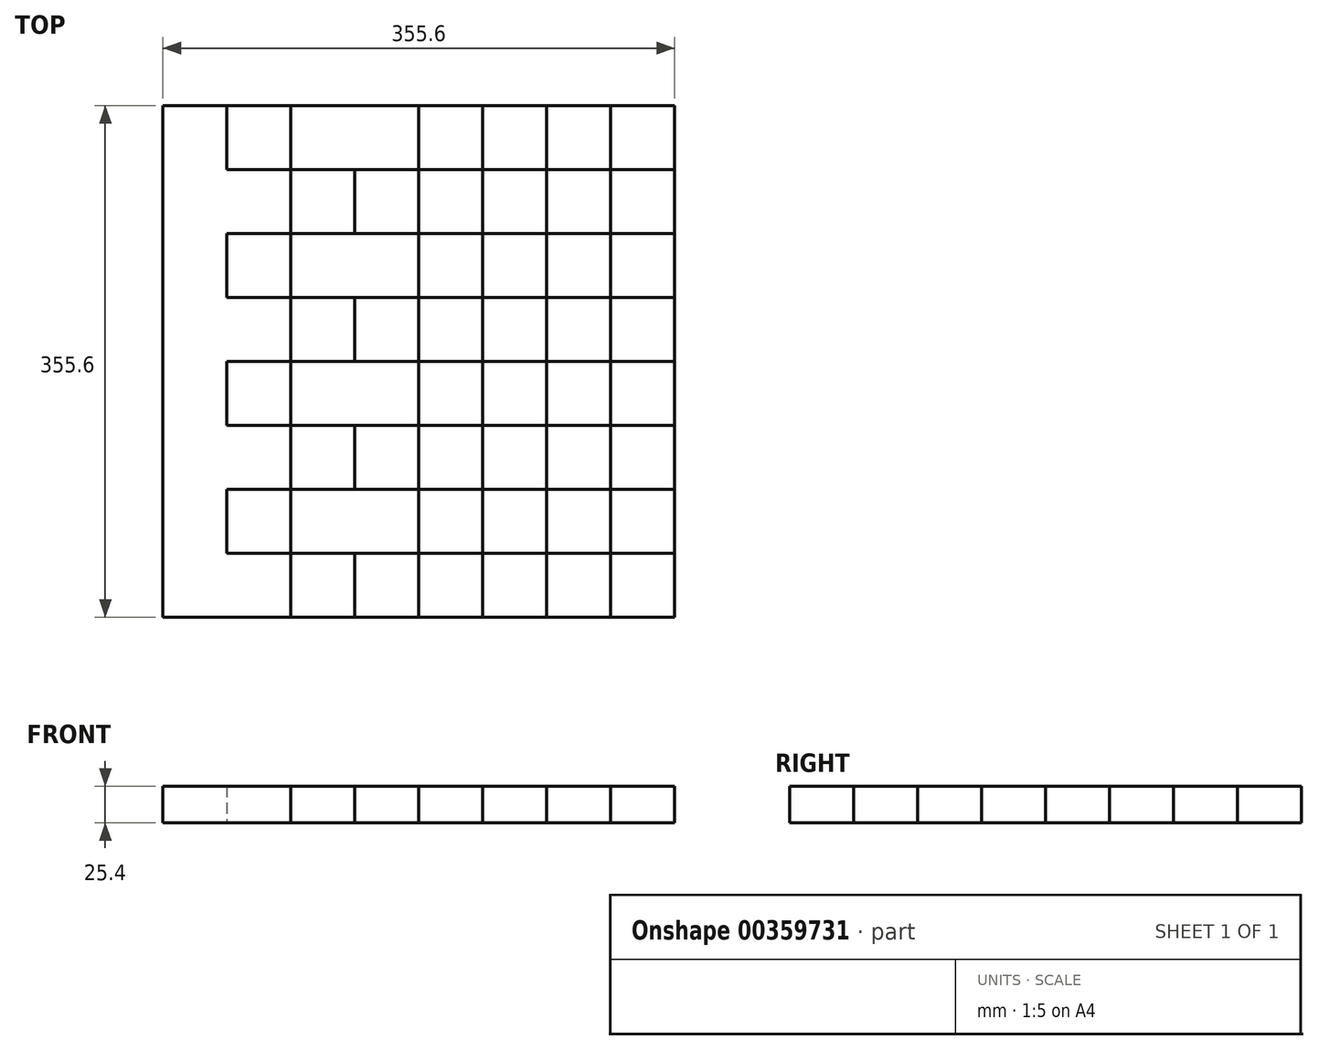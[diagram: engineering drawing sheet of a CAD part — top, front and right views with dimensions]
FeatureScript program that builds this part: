
annotation { "Feature Type Name" : "Feature", "Feature Type Description" : "" }
export const myFeature = defineFeature(function(context is Context, id is Id, definition is map)
    precondition{}
    {
        {
            var Q0;
            Q0=qCreatedBy(makeId("Top.planeOp"),FACE);
            var sketch = newSketch(context, id + "F0", { "sketchPlane" : qUnion([Q0])});
            skLineSegment(sketch, "E0.bottom", {"start": v(177.8, 177.8) * mm, "end": v(-177.8, 177.8) * mm});
            skLineSegment(sketch, "E0.top", {"start": v(177.8, -177.8) * mm, "end": v(-177.8, -177.8) * mm});
            skLineSegment(sketch, "E0.left", {"start": v(177.8, 177.8) * mm, "end": v(177.8, -177.8) * mm});
            skLineSegment(sketch, "E0.right", {"start": v(-177.8, 177.8) * mm, "end": v(-177.8, -177.8) * mm});
            skPoint(sketch, "E0.middle", {"position": v(0, 0) * mm});
            skLineSegment(sketch, "E1", {"start": v(-133.35, 177.8) * mm, "end": v(-133.35, -177.8) * mm});
            skLineSegment(sketch, "E2", {"start": v(-88.9, -177.8) * mm, "end": v(-88.9, 177.8) * mm});
            skLineSegment(sketch, "E3", {"start": v(-44.45, -177.8) * mm, "end": v(-44.45, 177.8) * mm});
            skLineSegment(sketch, "E4", {"start": v(0, 177.8) * mm, "end": v(0, -177.8) * mm});
            skLineSegment(sketch, "E5", {"start": v(0, -177.8) * mm, "end": v(0, 177.8) * mm});
            skLineSegment(sketch, "E6.MirrorCS", {"start": v(44.45, -177.8) * mm, "end": v(44.45, 177.8) * mm});
            skLineSegment(sketch, "E7.MirrorCS", {"start": v(88.9, -177.8) * mm, "end": v(88.9, 177.8) * mm});
            skLineSegment(sketch, "E8.MirrorCS", {"start": v(133.35, 177.8) * mm, "end": v(133.35, -177.8) * mm});
            skLineSegment(sketch, "E9", {"start": v(0, 0) * mm, "end": v(-177.8, 0) * mm});
            skLineSegment(sketch, "E10", {"start": v(-177.8, 0) * mm, "end": v(177.8, 0) * mm});
            skLineSegment(sketch, "E11", {"start": v(-177.8, 44.45) * mm, "end": v(177.8, 44.45) * mm});
            skLineSegment(sketch, "E12", {"start": v(177.8, 88.9) * mm, "end": v(-177.8, 88.9) * mm});
            skLineSegment(sketch, "E13", {"start": v(-177.8, 133.35) * mm, "end": v(177.8, 133.35) * mm});
            skLineSegment(sketch, "E14.MirrorCS", {"start": v(-177.8, -44.45) * mm, "end": v(177.8, -44.45) * mm});
            skLineSegment(sketch, "E15.MirrorCS", {"start": v(177.8, -88.9) * mm, "end": v(-177.8, -88.9) * mm});
            skLineSegment(sketch, "E16.MirrorCS", {"start": v(-177.8, -133.35) * mm, "end": v(177.8, -133.35) * mm});
            skSolve(sketch);
        }
        {
            var Q0;
            {var subQ0=sQuery(id+"F0.wireOp",EDGE,"E1");var subQ1=sQuery(id+"F0.wireOp",EDGE,"E0.top");var subQ2=makeQuery(id+"F0.imprint","INTERSECT",VERTEX,{"derivedFrom":[subQ1,subQ0]});Q0=makeQuery(id+"F0.imprint","IMPRINT",FACE,{"disambiguationData":[TD([[makeQuery(id+"F0.imprint","IMPRINT",EDGE,{"disambiguationData":[TD([[subQ2,1.0]])],"derivedFrom":subQ1}),-1.0]])]});}
            var Q1;
            {var subQ0=sQuery(id+"F0.wireOp",EDGE,"E3");var subQ1=sQuery(id+"F0.wireOp",EDGE,"E0.top");var subQ2=makeQuery(id+"F0.imprint","INTERSECT",VERTEX,{"derivedFrom":[subQ1,subQ0]});Q1=makeQuery(id+"F0.imprint","IMPRINT",FACE,{"disambiguationData":[TD([[makeQuery(id+"F0.imprint","IMPRINT",EDGE,{"disambiguationData":[TD([[subQ2,1.0]])],"derivedFrom":subQ1}),-1.0]])]});}
            var Q2;
            {var subQ0=sQuery(id+"F0.wireOp",EDGE,"E6.MirrorCS");var subQ1=sQuery(id+"F0.wireOp",EDGE,"E0.top");var subQ2=makeQuery(id+"F0.imprint","INTERSECT",VERTEX,{"derivedFrom":[subQ1,subQ0]});Q2=makeQuery(id+"F0.imprint","IMPRINT",FACE,{"disambiguationData":[TD([[makeQuery(id+"F0.imprint","IMPRINT",EDGE,{"disambiguationData":[TD([[subQ2,1.0]])],"derivedFrom":subQ1}),-1.0]])]});}
            var Q3;
            {var subQ0=sQuery(id+"F0.wireOp",EDGE,"E0.left");var subQ1=sQuery(id+"F0.wireOp",EDGE,"E0.top");var subQ2=makeQuery(id+"F0.imprint","INTERSECT",VERTEX,{"derivedFrom":[subQ1,subQ0]});Q3=makeQuery(id+"F0.imprint","IMPRINT",FACE,{"disambiguationData":[TD([[makeQuery(id+"F0.imprint","IMPRINT",EDGE,{"disambiguationData":[TD([[subQ2,-1.0]])],"derivedFrom":subQ1}),-1.0]])]});}
            var Q4;
            {var subQ0=sQuery(id+"F0.wireOp",EDGE,"E15.MirrorCS");var subQ1=sQuery(id+"F0.wireOp",EDGE,"E0.right");var subQ2=makeQuery(id+"F0.imprint","INTERSECT",VERTEX,{"derivedFrom":[subQ1,subQ0]});Q4=makeQuery(id+"F0.imprint","IMPRINT",FACE,{"disambiguationData":[TD([[makeQuery(id+"F0.imprint","IMPRINT",EDGE,{"disambiguationData":[TD([[subQ2,-1.0]])],"derivedFrom":subQ1}),1.0]])]});}
            var Q5;
            {var subQ0=sQuery(id+"F0.wireOp",EDGE,"E16.MirrorCS");var subQ1=sQuery(id+"F0.wireOp",EDGE,"E2");var subQ2=makeQuery(id+"F0.imprint","INTERSECT",VERTEX,{"derivedFrom":[subQ1,subQ0]});Q5=makeQuery(id+"F0.imprint","IMPRINT",FACE,{"disambiguationData":[TD([[makeQuery(id+"F0.imprint","IMPRINT",EDGE,{"disambiguationData":[TD([[subQ2,-1.0]])],"derivedFrom":subQ1}),-1.0]])]});}
            var Q6;
            {var subQ0=sQuery(id+"F0.wireOp",EDGE,"E15.MirrorCS");var subQ1=sQuery(id+"F0.wireOp",EDGE,"E4");var subQ2=makeQuery(id+"F0.imprint","INTERSECT",VERTEX,{"derivedFrom":[subQ1,subQ0]});Q6=makeQuery(id+"F0.imprint","IMPRINT",FACE,{"disambiguationData":[TD([[makeQuery(id+"F0.imprint","IMPRINT",EDGE,{"disambiguationData":[TD([[subQ2,-1.0]])],"derivedFrom":subQ1}),1.0]])]});}
            var Q7;
            {var subQ0=sQuery(id+"F0.wireOp",EDGE,"E16.MirrorCS");var subQ1=sQuery(id+"F0.wireOp",EDGE,"E7.MirrorCS");var subQ2=makeQuery(id+"F0.imprint","INTERSECT",VERTEX,{"derivedFrom":[subQ1,subQ0]});Q7=makeQuery(id+"F0.imprint","IMPRINT",FACE,{"disambiguationData":[TD([[makeQuery(id+"F0.imprint","IMPRINT",EDGE,{"disambiguationData":[TD([[subQ2,-1.0]])],"derivedFrom":subQ1}),-1.0]])]});}
            var Q8;
            {var subQ0=sQuery(id+"F0.wireOp",EDGE,"E14.MirrorCS");var subQ1=sQuery(id+"F0.wireOp",EDGE,"E0.left");var subQ2=makeQuery(id+"F0.imprint","INTERSECT",VERTEX,{"derivedFrom":[subQ1,subQ0]});Q8=makeQuery(id+"F0.imprint","IMPRINT",FACE,{"disambiguationData":[TD([[makeQuery(id+"F0.imprint","IMPRINT",EDGE,{"disambiguationData":[TD([[subQ2,-1.0]])],"derivedFrom":subQ1}),-1.0]])]});}
            var Q9;
            {var subQ0=sQuery(id+"F0.wireOp",EDGE,"E15.MirrorCS");var subQ1=sQuery(id+"F0.wireOp",EDGE,"E6.MirrorCS");var subQ2=makeQuery(id+"F0.imprint","INTERSECT",VERTEX,{"derivedFrom":[subQ1,subQ0]});Q9=makeQuery(id+"F0.imprint","IMPRINT",FACE,{"disambiguationData":[TD([[makeQuery(id+"F0.imprint","IMPRINT",EDGE,{"disambiguationData":[TD([[subQ2,-1.0]])],"derivedFrom":subQ1}),-1.0]])]});}
            var Q10;
            {var subQ0=sQuery(id+"F0.wireOp",EDGE,"E15.MirrorCS");var subQ1=sQuery(id+"F0.wireOp",EDGE,"E3");var subQ2=makeQuery(id+"F0.imprint","INTERSECT",VERTEX,{"derivedFrom":[subQ1,subQ0]});Q10=makeQuery(id+"F0.imprint","IMPRINT",FACE,{"disambiguationData":[TD([[makeQuery(id+"F0.imprint","IMPRINT",EDGE,{"disambiguationData":[TD([[subQ2,-1.0]])],"derivedFrom":subQ1}),-1.0]])]});}
            var Q11;
            {var subQ0=sQuery(id+"F0.wireOp",EDGE,"E14.MirrorCS");var subQ1=sQuery(id+"F0.wireOp",EDGE,"E1");var subQ2=makeQuery(id+"F0.imprint","INTERSECT",VERTEX,{"derivedFrom":[subQ1,subQ0]});Q11=makeQuery(id+"F0.imprint","IMPRINT",FACE,{"disambiguationData":[TD([[makeQuery(id+"F0.imprint","IMPRINT",EDGE,{"disambiguationData":[TD([[subQ2,-1.0]])],"derivedFrom":subQ1}),1.0]])]});}
            var Q12;
            {var subQ0=sQuery(id+"F0.wireOp",EDGE,"E10");var subQ1=sQuery(id+"F0.wireOp",EDGE,"E0.right");var subQ2=makeQuery(id+"F0.imprint","INTERSECT",VERTEX,{"derivedFrom":[subQ1,subQ0]});Q12=makeQuery(id+"F0.imprint","IMPRINT",FACE,{"disambiguationData":[TD([[makeQuery(id+"F0.imprint","IMPRINT",EDGE,{"disambiguationData":[TD([[subQ2,-1.0]])],"derivedFrom":subQ1}),1.0]])]});}
            var Q13;
            {var subQ0=sQuery(id+"F0.wireOp",EDGE,"E14.MirrorCS");var subQ1=sQuery(id+"F0.wireOp",EDGE,"E2");var subQ2=makeQuery(id+"F0.imprint","INTERSECT",VERTEX,{"derivedFrom":[subQ1,subQ0]});Q13=makeQuery(id+"F0.imprint","IMPRINT",FACE,{"disambiguationData":[TD([[makeQuery(id+"F0.imprint","IMPRINT",EDGE,{"disambiguationData":[TD([[subQ2,-1.0]])],"derivedFrom":subQ1}),-1.0]])]});}
            var Q14;
            {var subQ0=sQuery(id+"F0.wireOp",EDGE,"E10");var subQ1=sQuery(id+"F0.wireOp",EDGE,"E4");var subQ2=makeQuery(id+"F0.imprint","INTERSECT",VERTEX,{"derivedFrom":[subQ1,subQ0]});Q14=makeQuery(id+"F0.imprint","IMPRINT",FACE,{"disambiguationData":[TD([[makeQuery(id+"F0.imprint","IMPRINT",EDGE,{"disambiguationData":[TD([[subQ2,-1.0]])],"derivedFrom":subQ1}),1.0]])]});}
            var Q15;
            {var subQ0=sQuery(id+"F0.wireOp",EDGE,"E14.MirrorCS");var subQ1=sQuery(id+"F0.wireOp",EDGE,"E7.MirrorCS");var subQ2=makeQuery(id+"F0.imprint","INTERSECT",VERTEX,{"derivedFrom":[subQ1,subQ0]});Q15=makeQuery(id+"F0.imprint","IMPRINT",FACE,{"disambiguationData":[TD([[makeQuery(id+"F0.imprint","IMPRINT",EDGE,{"disambiguationData":[TD([[subQ2,-1.0]])],"derivedFrom":subQ1}),-1.0]])]});}
            var Q16;
            {var subQ0=sQuery(id+"F0.wireOp",EDGE,"E10");var subQ1=sQuery(id+"F0.wireOp",EDGE,"E0.left");var subQ2=makeQuery(id+"F0.imprint","INTERSECT",VERTEX,{"derivedFrom":[subQ1,subQ0]});Q16=makeQuery(id+"F0.imprint","IMPRINT",FACE,{"disambiguationData":[TD([[makeQuery(id+"F0.imprint","IMPRINT",EDGE,{"disambiguationData":[TD([[subQ2,1.0]])],"derivedFrom":subQ1}),-1.0]])]});}
            var Q17;
            {var subQ0=sQuery(id+"F0.wireOp",EDGE,"E10");var subQ1=sQuery(id+"F0.wireOp",EDGE,"E6.MirrorCS");var subQ2=makeQuery(id+"F0.imprint","INTERSECT",VERTEX,{"derivedFrom":[subQ1,subQ0]});Q17=makeQuery(id+"F0.imprint","IMPRINT",FACE,{"disambiguationData":[TD([[makeQuery(id+"F0.imprint","IMPRINT",EDGE,{"disambiguationData":[TD([[subQ2,-1.0]])],"derivedFrom":subQ1}),-1.0]])]});}
            var Q18;
            {var subQ0=sQuery(id+"F0.wireOp",EDGE,"E10");var subQ1=sQuery(id+"F0.wireOp",EDGE,"E3");var subQ2=makeQuery(id+"F0.imprint","INTERSECT",VERTEX,{"derivedFrom":[subQ1,subQ0]});Q18=makeQuery(id+"F0.imprint","IMPRINT",FACE,{"disambiguationData":[TD([[makeQuery(id+"F0.imprint","IMPRINT",EDGE,{"disambiguationData":[TD([[subQ2,-1.0]])],"derivedFrom":subQ1}),-1.0]])]});}
            var Q19;
            {var subQ0=sQuery(id+"F0.wireOp",EDGE,"E11");var subQ1=sQuery(id+"F0.wireOp",EDGE,"E1");var subQ2=makeQuery(id+"F0.imprint","INTERSECT",VERTEX,{"derivedFrom":[subQ1,subQ0]});Q19=makeQuery(id+"F0.imprint","IMPRINT",FACE,{"disambiguationData":[TD([[makeQuery(id+"F0.imprint","IMPRINT",EDGE,{"disambiguationData":[TD([[subQ2,-1.0]])],"derivedFrom":subQ1}),1.0]])]});}
            var Q20;
            {var subQ0=sQuery(id+"F0.wireOp",EDGE,"E11");var subQ1=sQuery(id+"F0.wireOp",EDGE,"E0.right");var subQ2=makeQuery(id+"F0.imprint","INTERSECT",VERTEX,{"derivedFrom":[subQ1,subQ0]});Q20=makeQuery(id+"F0.imprint","IMPRINT",FACE,{"disambiguationData":[TD([[makeQuery(id+"F0.imprint","IMPRINT",EDGE,{"disambiguationData":[TD([[subQ2,1.0]])],"derivedFrom":subQ1}),1.0]])]});}
            var Q21;
            {var subQ0=sQuery(id+"F0.wireOp",EDGE,"E11");var subQ1=sQuery(id+"F0.wireOp",EDGE,"E2");var subQ2=makeQuery(id+"F0.imprint","INTERSECT",VERTEX,{"derivedFrom":[subQ1,subQ0]});Q21=makeQuery(id+"F0.imprint","IMPRINT",FACE,{"disambiguationData":[TD([[makeQuery(id+"F0.imprint","IMPRINT",EDGE,{"disambiguationData":[TD([[subQ2,-1.0]])],"derivedFrom":subQ1}),-1.0]])]});}
            var Q22;
            {var subQ0=sQuery(id+"F0.wireOp",EDGE,"E12");var subQ1=sQuery(id+"F0.wireOp",EDGE,"E4");var subQ2=makeQuery(id+"F0.imprint","INTERSECT",VERTEX,{"derivedFrom":[subQ1,subQ0]});Q22=makeQuery(id+"F0.imprint","IMPRINT",FACE,{"disambiguationData":[TD([[makeQuery(id+"F0.imprint","IMPRINT",EDGE,{"disambiguationData":[TD([[subQ2,-1.0]])],"derivedFrom":subQ1}),1.0]])]});}
            var Q23;
            {var subQ0=sQuery(id+"F0.wireOp",EDGE,"E11");var subQ1=sQuery(id+"F0.wireOp",EDGE,"E7.MirrorCS");var subQ2=makeQuery(id+"F0.imprint","INTERSECT",VERTEX,{"derivedFrom":[subQ1,subQ0]});Q23=makeQuery(id+"F0.imprint","IMPRINT",FACE,{"disambiguationData":[TD([[makeQuery(id+"F0.imprint","IMPRINT",EDGE,{"disambiguationData":[TD([[subQ2,-1.0]])],"derivedFrom":subQ1}),-1.0]])]});}
            var Q24;
            {var subQ0=sQuery(id+"F0.wireOp",EDGE,"E12");var subQ1=sQuery(id+"F0.wireOp",EDGE,"E0.left");var subQ2=makeQuery(id+"F0.imprint","INTERSECT",VERTEX,{"derivedFrom":[subQ1,subQ0]});Q24=makeQuery(id+"F0.imprint","IMPRINT",FACE,{"disambiguationData":[TD([[makeQuery(id+"F0.imprint","IMPRINT",EDGE,{"disambiguationData":[TD([[subQ2,1.0]])],"derivedFrom":subQ1}),-1.0]])]});}
            var Q25;
            {var subQ0=sQuery(id+"F0.wireOp",EDGE,"E12");var subQ1=sQuery(id+"F0.wireOp",EDGE,"E6.MirrorCS");var subQ2=makeQuery(id+"F0.imprint","INTERSECT",VERTEX,{"derivedFrom":[subQ1,subQ0]});Q25=makeQuery(id+"F0.imprint","IMPRINT",FACE,{"disambiguationData":[TD([[makeQuery(id+"F0.imprint","IMPRINT",EDGE,{"disambiguationData":[TD([[subQ2,-1.0]])],"derivedFrom":subQ1}),-1.0]])]});}
            var Q26;
            {var subQ0=sQuery(id+"F0.wireOp",EDGE,"E12");var subQ1=sQuery(id+"F0.wireOp",EDGE,"E3");var subQ2=makeQuery(id+"F0.imprint","INTERSECT",VERTEX,{"derivedFrom":[subQ1,subQ0]});Q26=makeQuery(id+"F0.imprint","IMPRINT",FACE,{"disambiguationData":[TD([[makeQuery(id+"F0.imprint","IMPRINT",EDGE,{"disambiguationData":[TD([[subQ2,-1.0]])],"derivedFrom":subQ1}),-1.0]])]});}
            var Q27;
            {var subQ0=sQuery(id+"F0.wireOp",EDGE,"E13");var subQ1=sQuery(id+"F0.wireOp",EDGE,"E1");var subQ2=makeQuery(id+"F0.imprint","INTERSECT",VERTEX,{"derivedFrom":[subQ1,subQ0]});Q27=makeQuery(id+"F0.imprint","IMPRINT",FACE,{"disambiguationData":[TD([[makeQuery(id+"F0.imprint","IMPRINT",EDGE,{"disambiguationData":[TD([[subQ2,-1.0]])],"derivedFrom":subQ1}),1.0]])]});}
            var Q28;
            {var subQ0=sQuery(id+"F0.wireOp",EDGE,"E0.right");var subQ1=sQuery(id+"F0.wireOp",EDGE,"E0.bottom");var subQ2=makeQuery(id+"F0.imprint","INTERSECT",VERTEX,{"derivedFrom":[subQ1,subQ0]});Q28=makeQuery(id+"F0.imprint","IMPRINT",FACE,{"disambiguationData":[TD([[makeQuery(id+"F0.imprint","IMPRINT",EDGE,{"disambiguationData":[TD([[subQ2,1.0]])],"derivedFrom":subQ1}),1.0]])]});}
            var Q29;
            {var subQ0=sQuery(id+"F0.wireOp",EDGE,"E2");var subQ1=sQuery(id+"F0.wireOp",EDGE,"E0.bottom");var subQ2=makeQuery(id+"F0.imprint","INTERSECT",VERTEX,{"derivedFrom":[subQ1,subQ0]});Q29=makeQuery(id+"F0.imprint","IMPRINT",FACE,{"disambiguationData":[TD([[makeQuery(id+"F0.imprint","IMPRINT",EDGE,{"disambiguationData":[TD([[subQ2,1.0]])],"derivedFrom":subQ1}),1.0]])]});}
            var Q30;
            {var subQ0=sQuery(id+"F0.wireOp",EDGE,"E4");var subQ1=sQuery(id+"F0.wireOp",EDGE,"E0.bottom");var subQ2=makeQuery(id+"F0.imprint","INTERSECT",VERTEX,{"derivedFrom":[subQ1,subQ0]});Q30=makeQuery(id+"F0.imprint","IMPRINT",FACE,{"disambiguationData":[TD([[makeQuery(id+"F0.imprint","IMPRINT",EDGE,{"disambiguationData":[TD([[subQ2,1.0]])],"derivedFrom":subQ1}),1.0]])]});}
            var Q31;
            {var subQ0=sQuery(id+"F0.wireOp",EDGE,"E7.MirrorCS");var subQ1=sQuery(id+"F0.wireOp",EDGE,"E0.bottom");var subQ2=makeQuery(id+"F0.imprint","INTERSECT",VERTEX,{"derivedFrom":[subQ1,subQ0]});Q31=makeQuery(id+"F0.imprint","IMPRINT",FACE,{"disambiguationData":[TD([[makeQuery(id+"F0.imprint","IMPRINT",EDGE,{"disambiguationData":[TD([[subQ2,1.0]])],"derivedFrom":subQ1}),1.0]])]});}
            extrude(context, id + "F1", {"entities" : qUnion([Q0, Q1, Q2, Q3, Q4, Q5, Q6, Q7, Q8, Q9, Q10, Q11, Q12, Q13, Q14, Q15, Q16, Q17, Q18, Q19, Q20, Q21, Q22, Q23, Q24, Q25, Q26, Q27, Q28, Q29, Q30, Q31]), "depth" : 25.4 * mm});
        }
        {
            var Q0;
            {var subQ0=sQuery(id+"F0.wireOp",EDGE,"E1");var subQ1=sQuery(id+"F0.wireOp",EDGE,"E0.bottom");var subQ2=makeQuery(id+"F0.imprint","INTERSECT",VERTEX,{"derivedFrom":[subQ1,subQ0]});Q0=makeQuery(id+"F0.imprint","IMPRINT",FACE,{"disambiguationData":[TD([[makeQuery(id+"F0.imprint","IMPRINT",EDGE,{"disambiguationData":[TD([[subQ2,1.0]])],"derivedFrom":subQ1}),1.0]])]});}
            var Q1;
            {var subQ0=sQuery(id+"F0.wireOp",EDGE,"E12");var subQ1=sQuery(id+"F0.wireOp",EDGE,"E0.right");var subQ2=makeQuery(id+"F0.imprint","INTERSECT",VERTEX,{"derivedFrom":[subQ1,subQ0]});Q1=makeQuery(id+"F0.imprint","IMPRINT",FACE,{"disambiguationData":[TD([[makeQuery(id+"F0.imprint","IMPRINT",EDGE,{"disambiguationData":[TD([[subQ2,1.0]])],"derivedFrom":subQ1}),1.0]])]});}
            var Q2;
            {var subQ0=sQuery(id+"F0.wireOp",EDGE,"E12");var subQ1=sQuery(id+"F0.wireOp",EDGE,"E2");var subQ2=makeQuery(id+"F0.imprint","INTERSECT",VERTEX,{"derivedFrom":[subQ1,subQ0]});Q2=makeQuery(id+"F0.imprint","IMPRINT",FACE,{"disambiguationData":[TD([[makeQuery(id+"F0.imprint","IMPRINT",EDGE,{"disambiguationData":[TD([[subQ2,-1.0]])],"derivedFrom":subQ1}),-1.0]])]});}
            var Q3;
            {var subQ0=sQuery(id+"F0.wireOp",EDGE,"E3");var subQ1=sQuery(id+"F0.wireOp",EDGE,"E0.bottom");var subQ2=makeQuery(id+"F0.imprint","INTERSECT",VERTEX,{"derivedFrom":[subQ1,subQ0]});Q3=makeQuery(id+"F0.imprint","IMPRINT",FACE,{"disambiguationData":[TD([[makeQuery(id+"F0.imprint","IMPRINT",EDGE,{"disambiguationData":[TD([[subQ2,1.0]])],"derivedFrom":subQ1}),1.0]])]});}
            var Q4;
            {var subQ0=sQuery(id+"F0.wireOp",EDGE,"E13");var subQ1=sQuery(id+"F0.wireOp",EDGE,"E4");var subQ2=makeQuery(id+"F0.imprint","INTERSECT",VERTEX,{"derivedFrom":[subQ1,subQ0]});Q4=makeQuery(id+"F0.imprint","IMPRINT",FACE,{"disambiguationData":[TD([[makeQuery(id+"F0.imprint","IMPRINT",EDGE,{"disambiguationData":[TD([[subQ2,-1.0]])],"derivedFrom":subQ1}),1.0]])]});}
            var Q5;
            {var subQ0=sQuery(id+"F0.wireOp",EDGE,"E6.MirrorCS");var subQ1=sQuery(id+"F0.wireOp",EDGE,"E0.bottom");var subQ2=makeQuery(id+"F0.imprint","INTERSECT",VERTEX,{"derivedFrom":[subQ1,subQ0]});Q5=makeQuery(id+"F0.imprint","IMPRINT",FACE,{"disambiguationData":[TD([[makeQuery(id+"F0.imprint","IMPRINT",EDGE,{"disambiguationData":[TD([[subQ2,1.0]])],"derivedFrom":subQ1}),1.0]])]});}
            var Q6;
            {var subQ0=sQuery(id+"F0.wireOp",EDGE,"E0.left");var subQ1=sQuery(id+"F0.wireOp",EDGE,"E0.bottom");var subQ2=makeQuery(id+"F0.imprint","INTERSECT",VERTEX,{"derivedFrom":[subQ1,subQ0]});Q6=makeQuery(id+"F0.imprint","IMPRINT",FACE,{"disambiguationData":[TD([[makeQuery(id+"F0.imprint","IMPRINT",EDGE,{"disambiguationData":[TD([[subQ2,-1.0]])],"derivedFrom":subQ1}),1.0]])]});}
            var Q7;
            {var subQ0=sQuery(id+"F0.wireOp",EDGE,"E12");var subQ1=sQuery(id+"F0.wireOp",EDGE,"E7.MirrorCS");var subQ2=makeQuery(id+"F0.imprint","INTERSECT",VERTEX,{"derivedFrom":[subQ1,subQ0]});Q7=makeQuery(id+"F0.imprint","IMPRINT",FACE,{"disambiguationData":[TD([[makeQuery(id+"F0.imprint","IMPRINT",EDGE,{"disambiguationData":[TD([[subQ2,-1.0]])],"derivedFrom":subQ1}),-1.0]])]});}
            var Q8;
            {var subQ0=sQuery(id+"F0.wireOp",EDGE,"E11");var subQ1=sQuery(id+"F0.wireOp",EDGE,"E0.left");var subQ2=makeQuery(id+"F0.imprint","INTERSECT",VERTEX,{"derivedFrom":[subQ1,subQ0]});Q8=makeQuery(id+"F0.imprint","IMPRINT",FACE,{"disambiguationData":[TD([[makeQuery(id+"F0.imprint","IMPRINT",EDGE,{"disambiguationData":[TD([[subQ2,1.0]])],"derivedFrom":subQ1}),-1.0]])]});}
            var Q9;
            {var subQ0=sQuery(id+"F0.wireOp",EDGE,"E10");var subQ1=sQuery(id+"F0.wireOp",EDGE,"E7.MirrorCS");var subQ2=makeQuery(id+"F0.imprint","INTERSECT",VERTEX,{"derivedFrom":[subQ1,subQ0]});Q9=makeQuery(id+"F0.imprint","IMPRINT",FACE,{"disambiguationData":[TD([[makeQuery(id+"F0.imprint","IMPRINT",EDGE,{"disambiguationData":[TD([[subQ2,-1.0]])],"derivedFrom":subQ1}),-1.0]])]});}
            var Q10;
            {var subQ0=sQuery(id+"F0.wireOp",EDGE,"E11");var subQ1=sQuery(id+"F0.wireOp",EDGE,"E3");var subQ2=makeQuery(id+"F0.imprint","INTERSECT",VERTEX,{"derivedFrom":[subQ1,subQ0]});Q10=makeQuery(id+"F0.imprint","IMPRINT",FACE,{"disambiguationData":[TD([[makeQuery(id+"F0.imprint","IMPRINT",EDGE,{"disambiguationData":[TD([[subQ2,-1.0]])],"derivedFrom":subQ1}),-1.0]])]});}
            var Q11;
            {var subQ0=sQuery(id+"F0.wireOp",EDGE,"E12");var subQ1=sQuery(id+"F0.wireOp",EDGE,"E1");var subQ2=makeQuery(id+"F0.imprint","INTERSECT",VERTEX,{"derivedFrom":[subQ1,subQ0]});Q11=makeQuery(id+"F0.imprint","IMPRINT",FACE,{"disambiguationData":[TD([[makeQuery(id+"F0.imprint","IMPRINT",EDGE,{"disambiguationData":[TD([[subQ2,-1.0]])],"derivedFrom":subQ1}),1.0]])]});}
            var Q12;
            {var subQ0=sQuery(id+"F0.wireOp",EDGE,"E10");var subQ1=sQuery(id+"F0.wireOp",EDGE,"E2");var subQ2=makeQuery(id+"F0.imprint","INTERSECT",VERTEX,{"derivedFrom":[subQ1,subQ0]});Q12=makeQuery(id+"F0.imprint","IMPRINT",FACE,{"disambiguationData":[TD([[makeQuery(id+"F0.imprint","IMPRINT",EDGE,{"disambiguationData":[TD([[subQ2,-1.0]])],"derivedFrom":subQ1}),-1.0]])]});}
            var Q13;
            {var subQ0=sQuery(id+"F0.wireOp",EDGE,"E10");var subQ1=sQuery(id+"F0.wireOp",EDGE,"E0.right");var subQ2=makeQuery(id+"F0.imprint","INTERSECT",VERTEX,{"derivedFrom":[subQ1,subQ0]});Q13=makeQuery(id+"F0.imprint","IMPRINT",FACE,{"disambiguationData":[TD([[makeQuery(id+"F0.imprint","IMPRINT",EDGE,{"disambiguationData":[TD([[subQ2,1.0]])],"derivedFrom":subQ1}),1.0]])]});}
            var Q14;
            {var subQ0=sQuery(id+"F0.wireOp",EDGE,"E10");var subQ1=sQuery(id+"F0.wireOp",EDGE,"E1");var subQ2=makeQuery(id+"F0.imprint","INTERSECT",VERTEX,{"derivedFrom":[subQ1,subQ0]});Q14=makeQuery(id+"F0.imprint","IMPRINT",FACE,{"disambiguationData":[TD([[makeQuery(id+"F0.imprint","IMPRINT",EDGE,{"disambiguationData":[TD([[subQ2,-1.0]])],"derivedFrom":subQ1}),1.0]])]});}
            var Q15;
            {var subQ0=sQuery(id+"F0.wireOp",EDGE,"E14.MirrorCS");var subQ1=sQuery(id+"F0.wireOp",EDGE,"E0.right");var subQ2=makeQuery(id+"F0.imprint","INTERSECT",VERTEX,{"derivedFrom":[subQ1,subQ0]});Q15=makeQuery(id+"F0.imprint","IMPRINT",FACE,{"disambiguationData":[TD([[makeQuery(id+"F0.imprint","IMPRINT",EDGE,{"disambiguationData":[TD([[subQ2,-1.0]])],"derivedFrom":subQ1}),1.0]])]});}
            var Q16;
            {var subQ0=sQuery(id+"F0.wireOp",EDGE,"E15.MirrorCS");var subQ1=sQuery(id+"F0.wireOp",EDGE,"E2");var subQ2=makeQuery(id+"F0.imprint","INTERSECT",VERTEX,{"derivedFrom":[subQ1,subQ0]});Q16=makeQuery(id+"F0.imprint","IMPRINT",FACE,{"disambiguationData":[TD([[makeQuery(id+"F0.imprint","IMPRINT",EDGE,{"disambiguationData":[TD([[subQ2,-1.0]])],"derivedFrom":subQ1}),-1.0]])]});}
            var Q17;
            {var subQ0=sQuery(id+"F0.wireOp",EDGE,"E14.MirrorCS");var subQ1=sQuery(id+"F0.wireOp",EDGE,"E3");var subQ2=makeQuery(id+"F0.imprint","INTERSECT",VERTEX,{"derivedFrom":[subQ1,subQ0]});Q17=makeQuery(id+"F0.imprint","IMPRINT",FACE,{"disambiguationData":[TD([[makeQuery(id+"F0.imprint","IMPRINT",EDGE,{"disambiguationData":[TD([[subQ2,-1.0]])],"derivedFrom":subQ1}),-1.0]])]});}
            var Q18;
            {var subQ0=sQuery(id+"F0.wireOp",EDGE,"E14.MirrorCS");var subQ1=sQuery(id+"F0.wireOp",EDGE,"E4");var subQ2=makeQuery(id+"F0.imprint","INTERSECT",VERTEX,{"derivedFrom":[subQ1,subQ0]});Q18=makeQuery(id+"F0.imprint","IMPRINT",FACE,{"disambiguationData":[TD([[makeQuery(id+"F0.imprint","IMPRINT",EDGE,{"disambiguationData":[TD([[subQ2,-1.0]])],"derivedFrom":subQ1}),1.0]])]});}
            var Q19;
            {var subQ0=sQuery(id+"F0.wireOp",EDGE,"E14.MirrorCS");var subQ1=sQuery(id+"F0.wireOp",EDGE,"E6.MirrorCS");var subQ2=makeQuery(id+"F0.imprint","INTERSECT",VERTEX,{"derivedFrom":[subQ1,subQ0]});Q19=makeQuery(id+"F0.imprint","IMPRINT",FACE,{"disambiguationData":[TD([[makeQuery(id+"F0.imprint","IMPRINT",EDGE,{"disambiguationData":[TD([[subQ2,-1.0]])],"derivedFrom":subQ1}),-1.0]])]});}
            var Q20;
            {var subQ0=sQuery(id+"F0.wireOp",EDGE,"E15.MirrorCS");var subQ1=sQuery(id+"F0.wireOp",EDGE,"E7.MirrorCS");var subQ2=makeQuery(id+"F0.imprint","INTERSECT",VERTEX,{"derivedFrom":[subQ1,subQ0]});Q20=makeQuery(id+"F0.imprint","IMPRINT",FACE,{"disambiguationData":[TD([[makeQuery(id+"F0.imprint","IMPRINT",EDGE,{"disambiguationData":[TD([[subQ2,-1.0]])],"derivedFrom":subQ1}),-1.0]])]});}
            var Q21;
            {var subQ0=sQuery(id+"F0.wireOp",EDGE,"E15.MirrorCS");var subQ1=sQuery(id+"F0.wireOp",EDGE,"E0.left");var subQ2=makeQuery(id+"F0.imprint","INTERSECT",VERTEX,{"derivedFrom":[subQ1,subQ0]});Q21=makeQuery(id+"F0.imprint","IMPRINT",FACE,{"disambiguationData":[TD([[makeQuery(id+"F0.imprint","IMPRINT",EDGE,{"disambiguationData":[TD([[subQ2,-1.0]])],"derivedFrom":subQ1}),-1.0]])]});}
            var Q22;
            {var subQ0=sQuery(id+"F0.wireOp",EDGE,"E10");var subQ1=sQuery(id+"F0.wireOp",EDGE,"E0.left");var subQ2=makeQuery(id+"F0.imprint","INTERSECT",VERTEX,{"derivedFrom":[subQ1,subQ0]});Q22=makeQuery(id+"F0.imprint","IMPRINT",FACE,{"disambiguationData":[TD([[makeQuery(id+"F0.imprint","IMPRINT",EDGE,{"disambiguationData":[TD([[subQ2,-1.0]])],"derivedFrom":subQ1}),-1.0]])]});}
            var Q23;
            {var subQ0=sQuery(id+"F0.wireOp",EDGE,"E7.MirrorCS");var subQ1=sQuery(id+"F0.wireOp",EDGE,"E0.top");var subQ2=makeQuery(id+"F0.imprint","INTERSECT",VERTEX,{"derivedFrom":[subQ1,subQ0]});Q23=makeQuery(id+"F0.imprint","IMPRINT",FACE,{"disambiguationData":[TD([[makeQuery(id+"F0.imprint","IMPRINT",EDGE,{"disambiguationData":[TD([[subQ2,1.0]])],"derivedFrom":subQ1}),-1.0]])]});}
            var Q24;
            {var subQ0=sQuery(id+"F0.wireOp",EDGE,"E16.MirrorCS");var subQ1=sQuery(id+"F0.wireOp",EDGE,"E6.MirrorCS");var subQ2=makeQuery(id+"F0.imprint","INTERSECT",VERTEX,{"derivedFrom":[subQ1,subQ0]});Q24=makeQuery(id+"F0.imprint","IMPRINT",FACE,{"disambiguationData":[TD([[makeQuery(id+"F0.imprint","IMPRINT",EDGE,{"disambiguationData":[TD([[subQ2,-1.0]])],"derivedFrom":subQ1}),-1.0]])]});}
            var Q25;
            {var subQ0=sQuery(id+"F0.wireOp",EDGE,"E4");var subQ1=sQuery(id+"F0.wireOp",EDGE,"E0.top");var subQ2=makeQuery(id+"F0.imprint","INTERSECT",VERTEX,{"derivedFrom":[subQ1,subQ0]});Q25=makeQuery(id+"F0.imprint","IMPRINT",FACE,{"disambiguationData":[TD([[makeQuery(id+"F0.imprint","IMPRINT",EDGE,{"disambiguationData":[TD([[subQ2,1.0]])],"derivedFrom":subQ1}),-1.0]])]});}
            var Q26;
            {var subQ0=sQuery(id+"F0.wireOp",EDGE,"E16.MirrorCS");var subQ1=sQuery(id+"F0.wireOp",EDGE,"E3");var subQ2=makeQuery(id+"F0.imprint","INTERSECT",VERTEX,{"derivedFrom":[subQ1,subQ0]});Q26=makeQuery(id+"F0.imprint","IMPRINT",FACE,{"disambiguationData":[TD([[makeQuery(id+"F0.imprint","IMPRINT",EDGE,{"disambiguationData":[TD([[subQ2,-1.0]])],"derivedFrom":subQ1}),-1.0]])]});}
            var Q27;
            {var subQ0=sQuery(id+"F0.wireOp",EDGE,"E2");var subQ1=sQuery(id+"F0.wireOp",EDGE,"E0.top");var subQ2=makeQuery(id+"F0.imprint","INTERSECT",VERTEX,{"derivedFrom":[subQ1,subQ0]});Q27=makeQuery(id+"F0.imprint","IMPRINT",FACE,{"disambiguationData":[TD([[makeQuery(id+"F0.imprint","IMPRINT",EDGE,{"disambiguationData":[TD([[subQ2,1.0]])],"derivedFrom":subQ1}),-1.0]])]});}
            var Q28;
            {var subQ0=sQuery(id+"F0.wireOp",EDGE,"E15.MirrorCS");var subQ1=sQuery(id+"F0.wireOp",EDGE,"E1");var subQ2=makeQuery(id+"F0.imprint","INTERSECT",VERTEX,{"derivedFrom":[subQ1,subQ0]});Q28=makeQuery(id+"F0.imprint","IMPRINT",FACE,{"disambiguationData":[TD([[makeQuery(id+"F0.imprint","IMPRINT",EDGE,{"disambiguationData":[TD([[subQ2,-1.0]])],"derivedFrom":subQ1}),1.0]])]});}
            var Q29;
            {var subQ0=sQuery(id+"F0.wireOp",EDGE,"E0.right");var subQ1=sQuery(id+"F0.wireOp",EDGE,"E0.top");var subQ2=makeQuery(id+"F0.imprint","INTERSECT",VERTEX,{"derivedFrom":[subQ1,subQ0]});Q29=makeQuery(id+"F0.imprint","IMPRINT",FACE,{"disambiguationData":[TD([[makeQuery(id+"F0.imprint","IMPRINT",EDGE,{"disambiguationData":[TD([[subQ2,1.0]])],"derivedFrom":subQ1}),-1.0]])]});}
            var Q30;
            {var subQ0=sQuery(id+"F0.wireOp",EDGE,"E11");var subQ1=sQuery(id+"F0.wireOp",EDGE,"E4");var subQ2=makeQuery(id+"F0.imprint","INTERSECT",VERTEX,{"derivedFrom":[subQ1,subQ0]});Q30=makeQuery(id+"F0.imprint","IMPRINT",FACE,{"disambiguationData":[TD([[makeQuery(id+"F0.imprint","IMPRINT",EDGE,{"disambiguationData":[TD([[subQ2,-1.0]])],"derivedFrom":subQ1}),1.0]])]});}
            var Q31;
            {var subQ0=sQuery(id+"F0.wireOp",EDGE,"E11");var subQ1=sQuery(id+"F0.wireOp",EDGE,"E6.MirrorCS");var subQ2=makeQuery(id+"F0.imprint","INTERSECT",VERTEX,{"derivedFrom":[subQ1,subQ0]});Q31=makeQuery(id+"F0.imprint","IMPRINT",FACE,{"disambiguationData":[TD([[makeQuery(id+"F0.imprint","IMPRINT",EDGE,{"disambiguationData":[TD([[subQ2,-1.0]])],"derivedFrom":subQ1}),-1.0]])]});}
            extrude(context, id + "F2", {"entities" : qUnion([Q0, Q1, Q2, Q3, Q4, Q5, Q6, Q7, Q8, Q9, Q10, Q11, Q12, Q13, Q14, Q15, Q16, Q17, Q18, Q19, Q20, Q21, Q22, Q23, Q24, Q25, Q26, Q27, Q28, Q29, Q30, Q31]), "depth" : 25.4 * mm});
        }
    });
